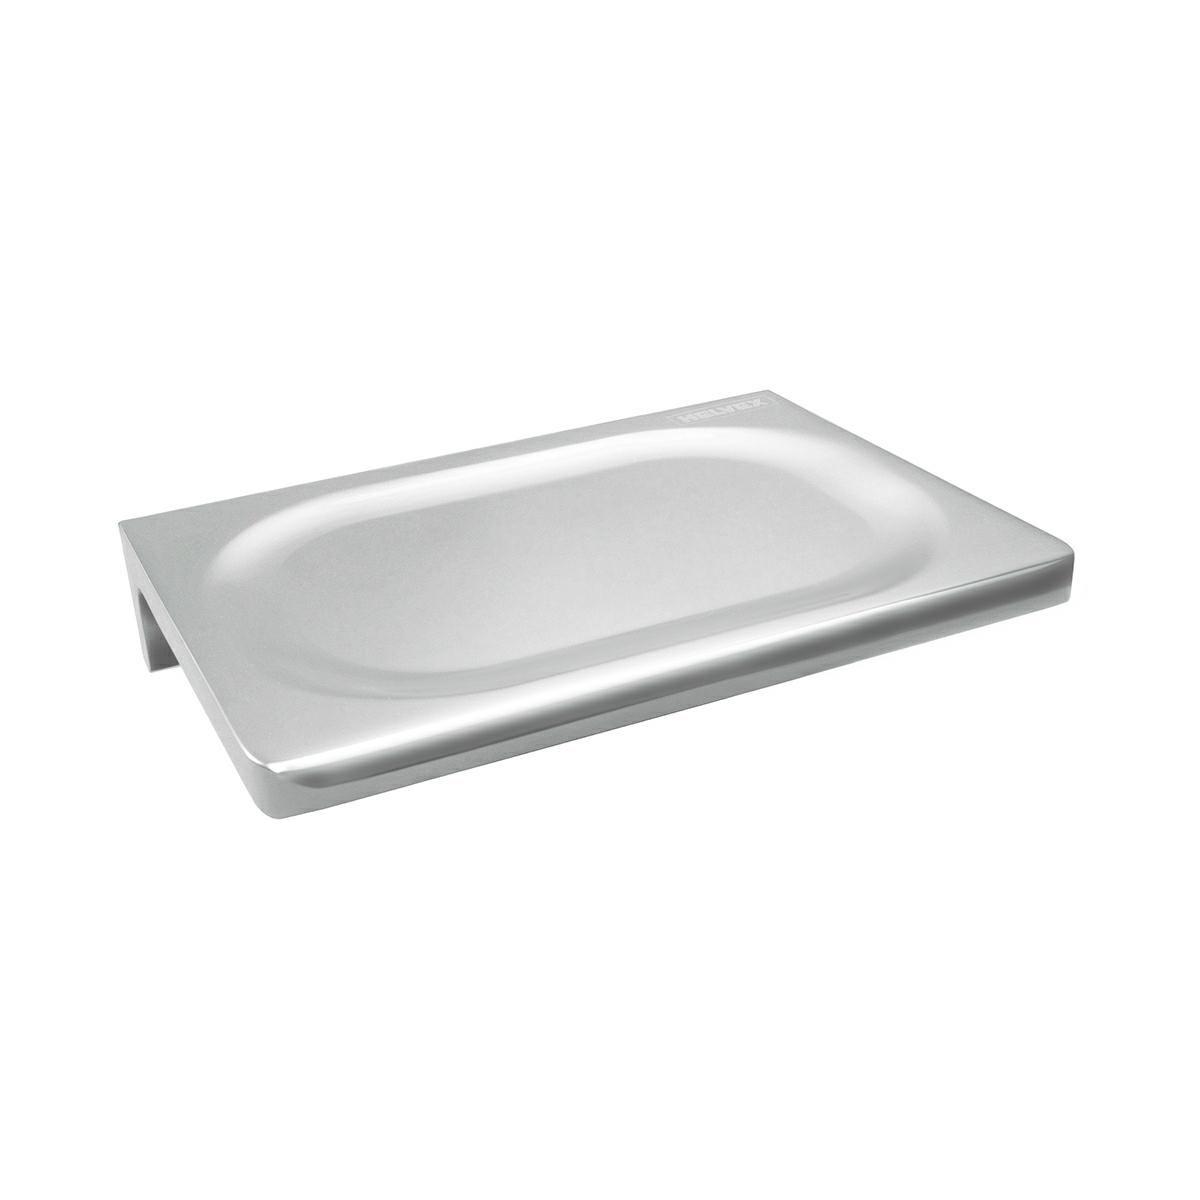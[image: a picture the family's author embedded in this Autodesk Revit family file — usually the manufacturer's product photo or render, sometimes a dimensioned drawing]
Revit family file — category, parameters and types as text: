
# Revit family: ACC-108_RFA
name_source: partatom
category: Aparatos sanitarios
units: mm (PartAtom-declared; Revit-internal decimal feet)

## family parameters
Compartido = No
Corte con vacíos al cargar = No
Cota de conector redondo = Diámetro de uso
Número OmniClass = 23.45.00.00
Punto de cálculo de habitación = No
Se basa en plano de trabajo = No
Siempre vertical = Sí
Tipo de pieza = Normal
Título OmniClass = Sanitary, Laundry, and Cleaning Equipment

## types (1)
- ACC-108
    Brass Chromed = Brass
    Comentarios de tipo = Accesorios
    Data Sheet = https://www.helvex.com.mx
    Descripción = Jabonera Access
    Elevación por defecto = 0"
    Fabricante = HELVEX
    Imagen de tipo = ACC-108.jpg
    Instructive = https://www.helvex.com.mx
    Modelo = ACC-108
    Niquel Duravex = Niquel Duravex
    Satin = Satin
    Total Depth = 5"
    Total Height = 2"
    Total Length = 5"
    Total Support Diameter = 2"
    URL = https://www.helvex.com.mx
    Ébano = Ébano

## geometry (parser evidence)
native form markers: Sweep x3
no freeform markers — native parametric forms only
